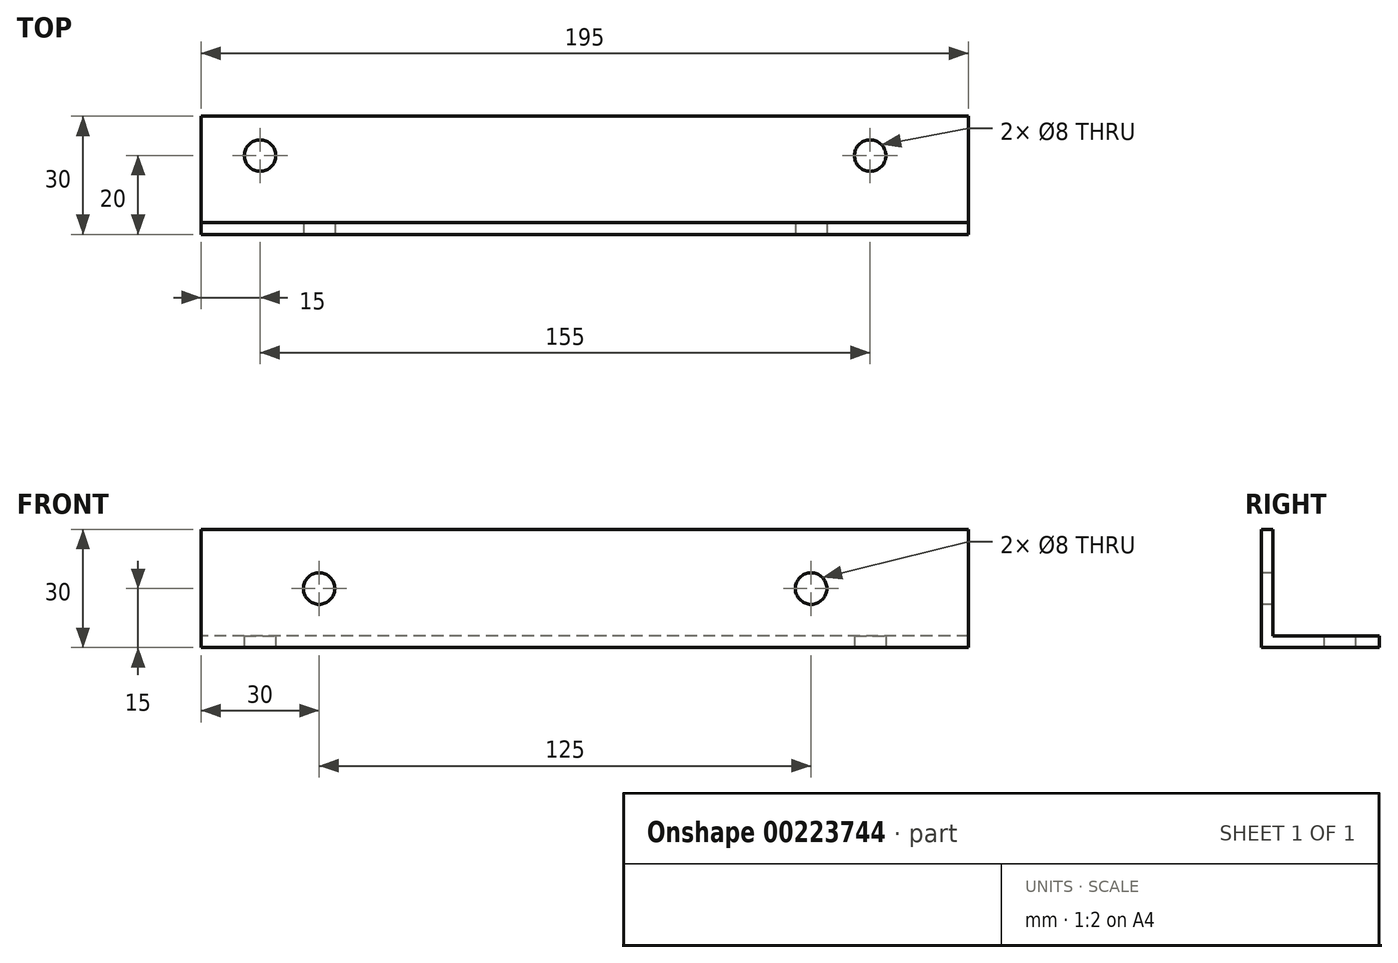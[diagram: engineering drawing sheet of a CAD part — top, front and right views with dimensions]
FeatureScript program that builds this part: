
annotation { "Feature Type Name" : "Feature", "Feature Type Description" : "" }
export const myFeature = defineFeature(function(context is Context, id is Id, definition is map)
    precondition{}
    {
        {
            var Q0;
            Q0=qCreatedBy(makeId("Right.planeOp"),FACE);
            var sketch = newSketch(context, id + "F0", { "sketchPlane" : qUnion([Q0])});
            skLineSegment(sketch, "E0", {"start": v(0, 0) * mm, "end": v(30, 0) * mm});
            skLineSegment(sketch, "E1", {"start": v(30, 0) * mm, "end": v(30, 3) * mm});
            skLineSegment(sketch, "E2", {"start": v(30, 3) * mm, "end": v(3, 3) * mm});
            skLineSegment(sketch, "E3", {"start": v(3, 3) * mm, "end": v(3, 30) * mm});
            skLineSegment(sketch, "E4", {"start": v(3, 30) * mm, "end": v(0, 30) * mm});
            skLineSegment(sketch, "E5", {"start": v(0, 30) * mm, "end": v(0, 0) * mm});
            skSolve(sketch);
        }
        {
            var Q0;
            Q0=qSketchRegion(id+"F0",true);
            extrude(context, id + "F1", {"entities" : qUnion([Q0]), "depth" : 195 * mm});
        }
        {
            var Q0;
            Q0=qCreatedBy(makeId("Top.planeOp"),FACE);
            var sketch = newSketch(context, id + "F2", { "sketchPlane" : qUnion([Q0])});
            skPoint(sketch, "E6", {"position": v(15, 20) * mm});
            skPoint(sketch, "E7", {"position": v(170, 20) * mm});
            skSolve(sketch);
        }
        {
            var Q0;
            Q0=sQuery(id+"F2.wireOp",VERTEX,"E6");
            var Q1;
            Q1=sQuery(id+"F2.wireOp",VERTEX,"E7");
            var Q2;
            Q2=makeQuery(id+"F1.opExtrude","SWEPT_BODY",BODY,{"disambiguationData":[OSD([sQuery(id+"F0.wireOp",EDGE,"E0"),sQuery(id+"F0.wireOp",EDGE,"E1"),sQuery(id+"F0.wireOp",EDGE,"E2"),sQuery(id+"F0.wireOp",EDGE,"E3"),sQuery(id+"F0.wireOp",EDGE,"E4"),sQuery(id+"F0.wireOp",EDGE,"E5")])]});
            hole(context, id + "F3", {"style" : HoleStyle.SIMPLE, "endStyle" : HoleEndStyle.THROUGH, "oppositeDirection" : true, "standardTappedOrClearance" : lookupTablePath({ "standard" : "ISO", "fit" : "Close", "size" : "M5", "type" : "Clearance" }), "standardBlindInLast" : lookupTablePath({ "fit" : "Close", "standard" : "ISO", "size" : "M5", "type" : "Clearance" }), "holeDiameter" : 8 * mm, "startFromSketch" : true, "locations" : qUnion([Q0, Q1]), "scope" : qUnion([Q2]), "isTappedThrough" : true});
        }
        {
            var Q0;
            Q0=qCreatedBy(makeId("Front.planeOp"),FACE);
            var sketch = newSketch(context, id + "F4", { "sketchPlane" : qUnion([Q0])});
            skPoint(sketch, "E8", {"position": v(155, 15) * mm});
            skPoint(sketch, "E9", {"position": v(30, 15) * mm});
            skSolve(sketch);
        }
        {
            var Q0;
            Q0=sQuery(id+"F4.wireOp",VERTEX,"E9");
            var Q1;
            Q1=sQuery(id+"F4.wireOp",VERTEX,"E8");
            var Q2;
            Q2=makeQuery(id+"F1.opExtrude","SWEPT_BODY",BODY,{"disambiguationData":[OSD([sQuery(id+"F0.wireOp",EDGE,"E0"),sQuery(id+"F0.wireOp",EDGE,"E1"),sQuery(id+"F0.wireOp",EDGE,"E2"),sQuery(id+"F0.wireOp",EDGE,"E3"),sQuery(id+"F0.wireOp",EDGE,"E4"),sQuery(id+"F0.wireOp",EDGE,"E5")])]});
            hole(context, id + "F5", {"style" : HoleStyle.SIMPLE, "endStyle" : HoleEndStyle.THROUGH, "holeDiameter" : 8 * mm, "startFromSketch" : true, "locations" : qUnion([Q0, Q1]), "scope" : qUnion([Q2]), "isTappedThrough" : true});
        }
    });
